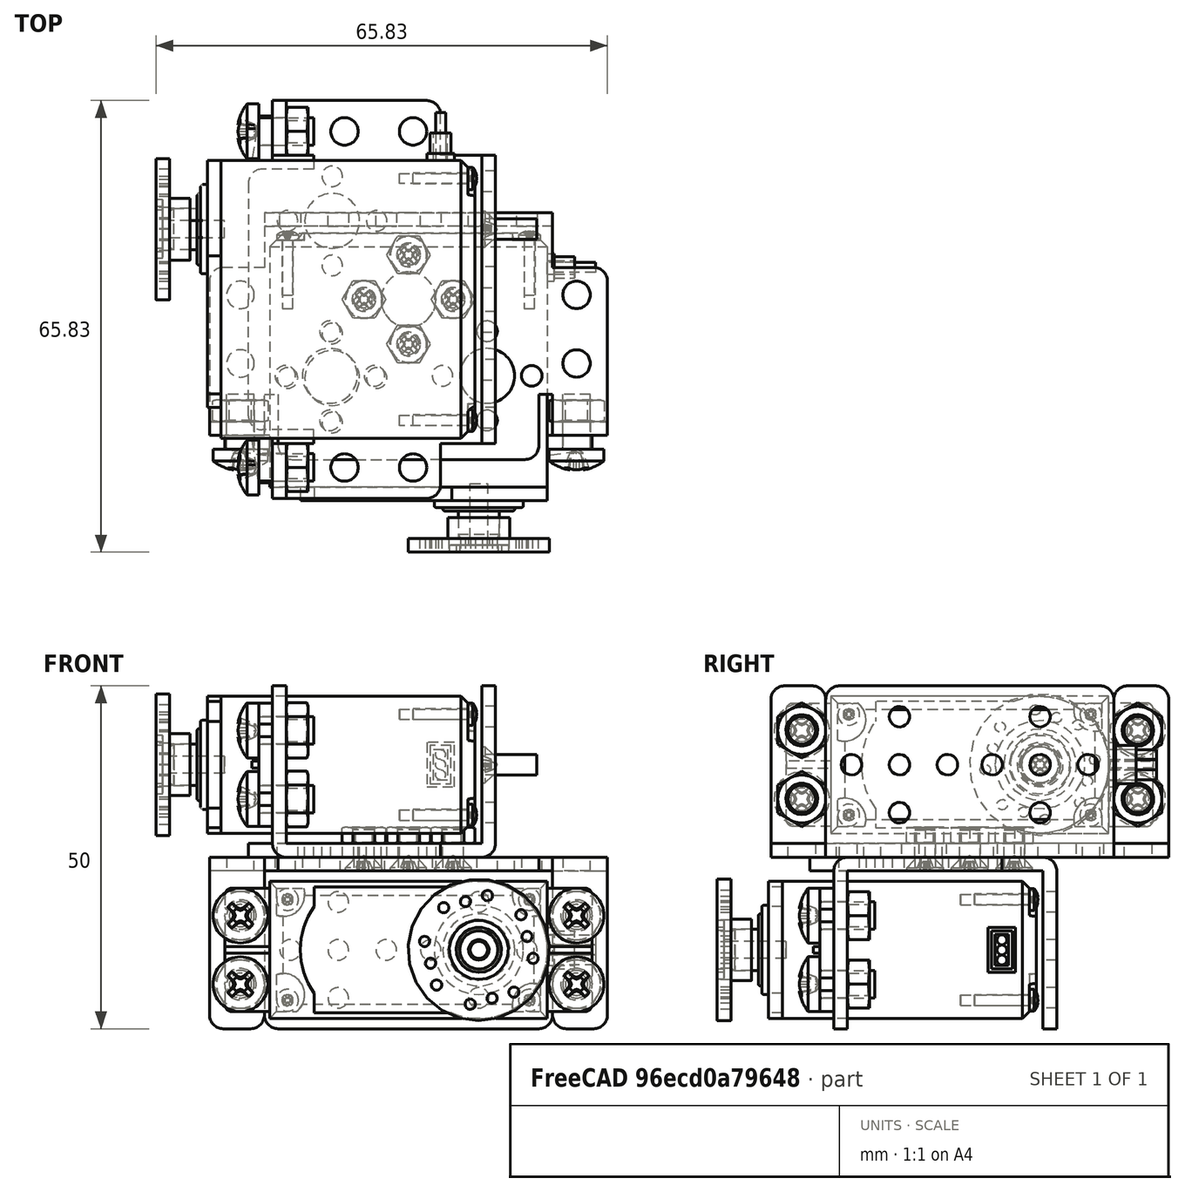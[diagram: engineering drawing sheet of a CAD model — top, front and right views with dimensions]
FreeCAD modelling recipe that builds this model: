
FCSTD DOCUMENT  (FreeCAD 0.19R24276 (Git))
Label: ante_mano
License: All rights reserved
LicenseURL: http://en.wikipedia.org/wiki/All_rights_reserved
objects: Part::FeaturePython×31, App::FeaturePython×24, App::DocumentObjectGroup×6
note: 31 computed .brp shape members not serialized (recipe doc carries the construction recipe); baked Part::Feature solids carry a one-line shape summary decoded from their .brp

FEATURE [Part::FeaturePython] b_parte_servos_001_  label="parte_servos_001"  # a2plus imported part (geometry in sourceFile) (typed FeaturePython)
  Placement = pos=(0,0,0) rot=(-1,0,0;3.14159rad)
  a2p_Version = V0.1
  fixedPosition = true
  objectType = a2pPart
  sourceFile = .\..\piezas\parte_servos.FCStd
  subassemblyImport = false
  timeLastImport = 1.62041e+09
  updateColors = true
FEATURE [Part::FeaturePython] b_parte_servos_001_001  label="parte_servos_002"  # a2plus imported part (geometry in sourceFile) (typed FeaturePython)
  Placement = pos=(-5.32887,5.32887,-1.3e-15) rot=(0,0,1;1.5708rad)
  a2p_Version = V0.1
  fixedPosition = false
  objectType = a2pPart
  sourceFile = .\..\piezas\parte_servos.FCStd
  subassemblyImport = false
  timeLastImport = 1.62041e+09
  updateColors = true
FEATURE [Part::FeaturePython] b_servo_001_  label="servo_001"  # a2plus imported part (geometry in sourceFile) (typed FeaturePython)
  Placement = pos=(2.47451e-08,15,-13.5) rot=(0,-0.707107,0.707107;3.14159rad)
  a2p_Version = V0.1
  fixedPosition = false
  objectType = a2pPart
  sourceFile = .\..\piezas\servo.FCStd
  subassemblyImport = false
  timeLastImport = 1.62041e+09
  updateColors = true
FEATURE [Part::FeaturePython] b_tapa_001_  label="tapa_001"  # a2plus imported part (geometry in sourceFile) (typed FeaturePython)
  Placement = pos=(10.25,-31.5,-13.5) rot=(-0.680531,0.518111,0.518111;1.94651rad)
  a2p_Version = V0.1
  fixedPosition = false
  objectType = a2pPart
  sourceFile = .\..\piezas\tapa.FCStd
  subassemblyImport = false
  timeLastImport = 1.62041e+09
  updateColors = true
FEATURE [App::FeaturePython] planeCoincident_002  label="planeCoincident_002__servo_001"  # a2plus constraint (typed FeaturePython)
  Object1 = b_tapa_001_
  Object2 = b_servo_001_
  ParentTreeObject = -> b_tapa_001_
  SubElement1 = Face23
  SubElement2 = Face7
  Suppressed = false
  Type = plane
  directionConstraint = 1
  offset = 0
FEATURE [App::FeaturePython] planeCoincident_002_mirror  label="planeCoincident_002__tapa_001"  # a2plus constraint (typed FeaturePython)
  Object1 = b_tapa_001_
  Object2 = b_servo_001_
  ParentTreeObject = -> b_servo_001_
  SubElement1 = Face23
  SubElement2 = Face7
  Suppressed = false
  Type = plane
  directionConstraint = 1
  offset = 0
FEATURE [App::FeaturePython] axisCoincident_002  label="axisCoincident_002__servo_001"  # a2plus constraint (typed FeaturePython)
  Object1 = b_tapa_001_
  Object2 = b_servo_001_
  ParentTreeObject = -> b_tapa_001_
  SubElement1 = Face21
  SubElement2 = Face3
  Suppressed = false
  Type = axial
  directionConstraint = 1
  lockRotation = false
FEATURE [App::FeaturePython] axisCoincident_002_mirror  label="axisCoincident_002__tapa_001"  # a2plus constraint (typed FeaturePython)
  Object1 = b_tapa_001_
  Object2 = b_servo_001_
  ParentTreeObject = -> b_servo_001_
  SubElement1 = Face21
  SubElement2 = Face3
  Suppressed = false
  Type = axial
  directionConstraint = 1
  lockRotation = false
FEATURE [App::FeaturePython] planeCoincident_003  label="planeCoincident_003__parte_servos_001"  # a2plus constraint (typed FeaturePython)
  Object1 = b_parte_servos_001_001
  Object2 = b_parte_servos_001_
  ParentTreeObject = -> b_parte_servos_001_001
  SubElement1 = Face8
  SubElement2 = Face8
  Suppressed = false
  Type = plane
  directionConstraint = 1
  offset = 0
FEATURE [App::FeaturePython] planeCoincident_003_mirror  label="planeCoincident_003__parte_servos_002"  # a2plus constraint (typed FeaturePython)
  Object1 = b_parte_servos_001_001
  Object2 = b_parte_servos_001_
  ParentTreeObject = -> b_parte_servos_001_
  SubElement1 = Face8
  SubElement2 = Face8
  Suppressed = false
  Type = plane
  directionConstraint = 1
  offset = 0
FEATURE [App::FeaturePython] axisCoincident_001  label="axisCoincident_001__servo_001"  # a2plus constraint (typed FeaturePython)
  Object1 = b_parte_servos_001_
  Object2 = b_servo_001_
  ParentTreeObject = -> b_parte_servos_001_
  SubElement1 = Face82
  SubElement2 = Face81
  Suppressed = false
  Type = axial
  directionConstraint = 0
  lockRotation = false
FEATURE [App::FeaturePython] axisCoincident_001_mirror  label="axisCoincident_001__parte_servos_001"  # a2plus constraint (typed FeaturePython)
  Object1 = b_parte_servos_001_
  Object2 = b_servo_001_
  ParentTreeObject = -> b_servo_001_
  SubElement1 = Face82
  SubElement2 = Face81
  Suppressed = false
  Type = axial
  directionConstraint = 0
  lockRotation = false
FEATURE [App::FeaturePython] axisCoincident_005  label="axisCoincident_005__parte_servos_001"  # a2plus constraint (typed FeaturePython)
  Object1 = b_servo_001_
  Object2 = b_parte_servos_001_
  ParentTreeObject = -> b_servo_001_
  SubElement1 = Face64
  SubElement2 = Face74
  Suppressed = false
  Type = axial
  directionConstraint = 0
  lockRotation = false
FEATURE [App::FeaturePython] axisCoincident_005_mirror  label="axisCoincident_005__servo_001"  # a2plus constraint (typed FeaturePython)
  Object1 = b_servo_001_
  Object2 = b_parte_servos_001_
  ParentTreeObject = -> b_parte_servos_001_
  SubElement1 = Face64
  SubElement2 = Face74
  Suppressed = false
  Type = axial
  directionConstraint = 0
  lockRotation = false
FEATURE [Part::FeaturePython] b_servo_001_001  label="servo_002"  # a2plus imported part (geometry in sourceFile) (typed FeaturePython)
  Placement = pos=(9.67113,5.32887,13.5) rot=(-0.57735,0.57735,0.57735;4.18879rad)
  a2p_Version = V0.1
  fixedPosition = false
  objectType = a2pPart
  sourceFile = .\..\piezas\servo.FCStd
  subassemblyImport = false
  timeLastImport = 1.62041e+09
  updateColors = true
FEATURE [Part::FeaturePython] b_tapa_001_001  label="tapa_002"  # a2plus imported part (geometry in sourceFile) (typed FeaturePython)
  Placement = pos=(-36.8289,15.5789,13.5) rot=(0.631714,-0.449306,0.631714;3.98615rad)
  a2p_Version = V0.1
  fixedPosition = false
  objectType = a2pPart
  sourceFile = .\..\piezas\tapa.FCStd
  subassemblyImport = false
  timeLastImport = 1.62041e+09
  updateColors = true
FEATURE [App::FeaturePython] planeCoincident_001  label="planeCoincident_001__servo_002"  # a2plus constraint (typed FeaturePython)
  Object1 = b_parte_servos_001_001
  Object2 = b_servo_001_001
  ParentTreeObject = -> b_parte_servos_001_001
  SubElement1 = Face84
  SubElement2 = Face34
  Suppressed = false
  Type = plane
  directionConstraint = 1
  offset = 0
FEATURE [App::FeaturePython] planeCoincident_001_mirror  label="planeCoincident_001__parte_servos_002"  # a2plus constraint (typed FeaturePython)
  Object1 = b_parte_servos_001_001
  Object2 = b_servo_001_001
  ParentTreeObject = -> b_servo_001_001
  SubElement1 = Face84
  SubElement2 = Face34
  Suppressed = false
  Type = plane
  directionConstraint = 1
  offset = 0
FEATURE [App::FeaturePython] planeCoincident_004  label="planeCoincident_004__tapa_002"  # a2plus constraint (typed FeaturePython)
  Object1 = b_servo_001_001
  Object2 = b_tapa_001_001
  ParentTreeObject = -> b_servo_001_001
  SubElement1 = Face118
  SubElement2 = Face23
  Suppressed = false
  Type = plane
  directionConstraint = 1
  offset = 0
FEATURE [App::FeaturePython] planeCoincident_004_mirror  label="planeCoincident_004__servo_002"  # a2plus constraint (typed FeaturePython)
  Object1 = b_servo_001_001
  Object2 = b_tapa_001_001
  ParentTreeObject = -> b_tapa_001_001
  SubElement1 = Face118
  SubElement2 = Face23
  Suppressed = false
  Type = plane
  directionConstraint = 1
  offset = 0
FEATURE [App::FeaturePython] axisCoincident_008  label="axisCoincident_008__servo_002"  # a2plus constraint (typed FeaturePython)
  Object1 = b_tapa_001_001
  Object2 = b_servo_001_001
  ParentTreeObject = -> b_tapa_001_001
  SubElement1 = Face21
  SubElement2 = Face3
  Suppressed = false
  Type = axial
  directionConstraint = 1
  lockRotation = false
FEATURE [App::FeaturePython] axisCoincident_008_mirror  label="axisCoincident_008__tapa_002"  # a2plus constraint (typed FeaturePython)
  Object1 = b_tapa_001_001
  Object2 = b_servo_001_001
  ParentTreeObject = -> b_servo_001_001
  SubElement1 = Face21
  SubElement2 = Face3
  Suppressed = false
  Type = axial
  directionConstraint = 1
  lockRotation = false
FEATURE [Part::FeaturePython] Screw004  label="M4x8-Screw004"  # Fasteners workbench fastener (typed FeaturePython)
  Placement = pos=(24.5,-16.5,-18.5) rot=(1,0,0;1.5708rad)
  baseObject = -> b_servo_001_ [Edge136]
  diameter = 6
  invert = true
  length = 12
  lengthCustom = 8
  matchOuter = true
  offset = 0
  thread = false
  type = 34
FEATURE [Part::FeaturePython] Screw005  label="M4x8-Screw005"  # Fasteners workbench fastener (typed FeaturePython)
  Placement = pos=(24.5,-16.5,-8.5) rot=(1,0,0;1.5708rad)
  baseObject = -> b_servo_001_ [Edge162]
  diameter = 6
  invert = true
  length = 12
  lengthCustom = 8
  matchOuter = true
  offset = 0
  thread = false
  type = 34
FEATURE [Part::FeaturePython] Screw006  label="M4x8-Screw006"  # Fasteners workbench fastener (typed FeaturePython)
  Placement = pos=(-24.5,-16.5,-18.5) rot=(1,0,0;1.5708rad)
  baseObject = -> b_servo_001_ [Edge606]
  diameter = 6
  invert = false
  length = 12
  lengthCustom = 8
  matchOuter = true
  offset = 0
  thread = false
  type = 34
FEATURE [Part::FeaturePython] Screw007  label="M4x8-Screw007"  # Fasteners workbench fastener (typed FeaturePython)
  Placement = pos=(-24.5,-16.5,-8.5) rot=(1,0,0;1.5708rad)
  baseObject = -> b_servo_001_ [Edge361]
  diameter = 6
  invert = false
  length = 12
  lengthCustom = 8
  matchOuter = true
  offset = 0
  thread = false
  type = 34
FEATURE [App::DocumentObjectGroup] Group003  label="parte2"
  Group = -> [Screw004,Screw005,Screw006,Screw007]
FEATURE [App::FeaturePython] axisCoincident_006  label="axisCoincident_006__parte_servos_002"  # a2plus constraint (typed FeaturePython)
  Object1 = b_servo_001_001
  Object2 = b_parte_servos_001_001
  ParentTreeObject = -> b_servo_001_001
  SubElement1 = Face73
  SubElement2 = Face81
  Suppressed = false
  Type = axial
  directionConstraint = 0
  lockRotation = false
FEATURE [App::FeaturePython] axisCoincident_006_mirror  label="axisCoincident_006__servo_002"  # a2plus constraint (typed FeaturePython)
  Object1 = b_servo_001_001
  Object2 = b_parte_servos_001_001
  ParentTreeObject = -> b_parte_servos_001_001
  SubElement1 = Face73
  SubElement2 = Face81
  Suppressed = false
  Type = axial
  directionConstraint = 0
  lockRotation = false
FEATURE [App::FeaturePython] axisCoincident_007  label="axisCoincident_007__parte_servos_002"  # a2plus constraint (typed FeaturePython)
  Object1 = b_servo_001_001
  Object2 = b_parte_servos_001_001
  ParentTreeObject = -> b_servo_001_001
  SubElement1 = Face64
  SubElement2 = Face74
  Suppressed = false
  Type = axial
  directionConstraint = 0
  lockRotation = false
FEATURE [App::FeaturePython] axisCoincident_007_mirror  label="axisCoincident_007__servo_002"  # a2plus constraint (typed FeaturePython)
  Object1 = b_servo_001_001
  Object2 = b_parte_servos_001_001
  ParentTreeObject = -> b_parte_servos_001_001
  SubElement1 = Face64
  SubElement2 = Face74
  Suppressed = false
  Type = axial
  directionConstraint = 0
  lockRotation = false
FEATURE [App::FeaturePython] axisCoincident_003  label="axisCoincident_003__parte_servos_002"  # a2plus constraint (typed FeaturePython)
  Object1 = b_parte_servos_001_
  Object2 = b_parte_servos_001_001
  ParentTreeObject = -> b_parte_servos_001_
  SubElement1 = Face29
  SubElement2 = Face58
  Suppressed = false
  Type = axial
  directionConstraint = 1
  lockRotation = false
FEATURE [App::FeaturePython] axisCoincident_003_mirror  label="axisCoincident_003__parte_servos_001"  # a2plus constraint (typed FeaturePython)
  Object1 = b_parte_servos_001_
  Object2 = b_parte_servos_001_001
  ParentTreeObject = -> b_parte_servos_001_001
  SubElement1 = Face29
  SubElement2 = Face58
  Suppressed = false
  Type = axial
  directionConstraint = 1
  lockRotation = false
FEATURE [App::FeaturePython] axisCoincident_004  label="axisCoincident_004__parte_servos_001"  # a2plus constraint (typed FeaturePython)
  Object1 = b_parte_servos_001_001
  Object2 = b_parte_servos_001_
  ParentTreeObject = -> b_parte_servos_001_001
  SubElement1 = Face40
  SubElement2 = Face33
  Suppressed = false
  Type = axial
  directionConstraint = 1
  lockRotation = false
FEATURE [App::FeaturePython] axisCoincident_004_mirror  label="axisCoincident_004__parte_servos_002"  # a2plus constraint (typed FeaturePython)
  Object1 = b_parte_servos_001_001
  Object2 = b_parte_servos_001_
  ParentTreeObject = -> b_parte_servos_001_
  SubElement1 = Face40
  SubElement2 = Face33
  Suppressed = false
  Type = axial
  directionConstraint = 1
  lockRotation = false
FEATURE [Part::FeaturePython] Screw  label="M4x8-Screw"  # Fasteners workbench fastener (typed FeaturePython)
  Placement = pos=(-21.8289,29.8289,8.5) rot=(0,-1,0;1.5708rad)
  baseObject = -> b_servo_001_001 [Edge421]
  diameter = 6
  invert = true
  length = 12
  lengthCustom = 8
  matchOuter = true
  offset = 0
  thread = false
  type = 34
FEATURE [Part::FeaturePython] Screw013  label="M4x8-Screw001"  # Fasteners workbench fastener (typed FeaturePython)
  Placement = pos=(-21.8289,-19.1711,8.5) rot=(0,-1,0;1.5708rad)
  baseObject = -> b_servo_001_001 [Edge102]
  diameter = 6
  invert = false
  length = 12
  lengthCustom = 8
  matchOuter = true
  offset = 0
  thread = false
  type = 34
FEATURE [Part::FeaturePython] Screw014  label="M4x8-Screw002"  # Fasteners workbench fastener (typed FeaturePython)
  Placement = pos=(-21.8289,-19.1711,18.5) rot=(0,-1,0;1.5708rad)
  baseObject = -> b_servo_001_001 [Edge88]
  diameter = 6
  invert = false
  length = 12
  lengthCustom = 8
  matchOuter = true
  offset = 0
  thread = false
  type = 34
FEATURE [Part::FeaturePython] Screw015  label="M4x8-Screw003"  # Fasteners workbench fastener (typed FeaturePython)
  Placement = pos=(-21.8289,29.8289,18.5) rot=(0,-1,0;1.5708rad)
  baseObject = -> b_servo_001_001 [Edge395]
  diameter = 6
  invert = true
  length = 12
  lengthCustom = 8
  matchOuter = true
  offset = 0
  thread = false
  type = 34
FEATURE [App::DocumentObjectGroup] Group002  label="parte1"
  Group = -> [Screw,Screw013,Screw014,Screw015]
FEATURE [Part::FeaturePython] Screw016  label="M3x6-Screw"  # Fasteners workbench fastener (typed FeaturePython)
  Placement = pos=(0,11.8289,-2) rot=(-1,0,0;3.14159rad)
  baseObject = -> b_parte_servos_001_ [Edge148]
  diameter = 4
  invert = false
  length = 11
  lengthCustom = 6
  matchOuter = false
  offset = 0
  thread = false
  type = 35
FEATURE [Part::FeaturePython] Screw017  label="M3x6-Screw001"  # Fasteners workbench fastener (typed FeaturePython)
  Placement = pos=(6.5,5.32887,-2) rot=(-1,0,0;3.14159rad)
  baseObject = -> b_parte_servos_001_ [Edge154]
  diameter = 4
  invert = false
  length = 11
  lengthCustom = 6
  matchOuter = false
  offset = 0
  thread = false
  type = 35
FEATURE [Part::FeaturePython] Screw018  label="M3x6-Screw002"  # Fasteners workbench fastener (typed FeaturePython)
  Placement = pos=(0,-1.17113,-2) rot=(-1,0,0;3.14159rad)
  baseObject = -> b_parte_servos_001_ [Edge152]
  diameter = 4
  invert = false
  length = 11
  lengthCustom = 6
  matchOuter = false
  offset = 0
  thread = false
  type = 35
FEATURE [Part::FeaturePython] Screw019  label="M3x6-Screw003"  # Fasteners workbench fastener (typed FeaturePython)
  Placement = pos=(-6.5,5.32887,-2) rot=(-1,0,0;3.14159rad)
  baseObject = -> b_parte_servos_001_ [Edge106]
  diameter = 4
  invert = false
  length = 11
  lengthCustom = 6
  matchOuter = false
  offset = 0
  thread = false
  type = 35
FEATURE [Part::FeaturePython] Nut  label="M4-Nut"  # Fasteners workbench fastener (typed FeaturePython)
  Placement = pos=(-17.8289,-19.1711,8.5) rot=(0,1,0;1.5708rad)
  baseObject = -> b_parte_servos_001_001 [Edge193]
  diameter = 6
  invert = true
  matchOuter = true
  offset = 0
  thread = false
  type = 7
FEATURE [Part::FeaturePython] Nut001  label="M4-Nut001"  # Fasteners workbench fastener (typed FeaturePython)
  Placement = pos=(-17.8289,-19.1711,18.5) rot=(0,1,0;1.5708rad)
  baseObject = -> b_parte_servos_001_001 [Edge192]
  diameter = 6
  invert = true
  matchOuter = true
  offset = 0
  thread = false
  type = 7
FEATURE [Part::FeaturePython] Nut002  label="M4-Nut002"  # Fasteners workbench fastener (typed FeaturePython)
  Placement = pos=(-17.8289,29.8289,8.5) rot=(0,1,0;1.5708rad)
  baseObject = -> b_parte_servos_001_001 [Edge220]
  diameter = 6
  invert = true
  matchOuter = true
  offset = 0
  thread = false
  type = 7
FEATURE [Part::FeaturePython] Nut003  label="M4-Nut003"  # Fasteners workbench fastener (typed FeaturePython)
  Placement = pos=(-17.8289,29.8289,18.5) rot=(0,1,0;1.5708rad)
  baseObject = -> b_parte_servos_001_001 [Edge219]
  diameter = 6
  invert = true
  matchOuter = true
  offset = 0
  thread = false
  type = 7
FEATURE [App::DocumentObjectGroup] Group004  label="parte_1"
  Group = -> [Nut,Nut001,Nut002,Nut003]
FEATURE [Part::FeaturePython] Nut004  label="M3-Nut"  # Fasteners workbench fastener (typed FeaturePython)
  Placement = pos=(6.5,5.32887,2) rot=(0,0,1;0rad)
  baseObject = -> b_parte_servos_001_001 [Edge100]
  diameter = 4
  invert = false
  matchOuter = true
  offset = 0
  thread = false
  type = 7
FEATURE [Part::FeaturePython] Nut005  label="M3-Nut001"  # Fasteners workbench fastener (typed FeaturePython)
  Placement = pos=(5.23036e-07,-1.17113,2) rot=(0,0,1;0rad)
  baseObject = -> b_parte_servos_001_001 [Edge106]
  diameter = 4
  invert = false
  matchOuter = true
  offset = 0
  thread = false
  type = 7
FEATURE [Part::FeaturePython] Nut006  label="M3-Nut002"  # Fasteners workbench fastener (typed FeaturePython)
  Placement = pos=(-6.5,5.32887,2) rot=(0,0,1;0rad)
  baseObject = -> b_parte_servos_001_001 [Edge104]
  diameter = 4
  invert = false
  matchOuter = true
  offset = 0
  thread = false
  type = 7
FEATURE [Part::FeaturePython] Nut007  label="M3-Nut003"  # Fasteners workbench fastener (typed FeaturePython)
  Placement = pos=(6.88169e-07,11.8289,2) rot=(0,0,1;0rad)
  baseObject = -> b_parte_servos_001_001 [Edge154]
  diameter = 4
  invert = false
  matchOuter = true
  offset = 0
  thread = false
  type = 7
FEATURE [Part::FeaturePython] Nut008  label="M4-Nut004"  # Fasteners workbench fastener (typed FeaturePython)
  Placement = pos=(24.5,-12.5,-8.5) rot=(-1,0,0;1.5708rad)
  baseObject = -> b_parte_servos_001_ [Edge220]
  diameter = 6
  invert = true
  matchOuter = true
  offset = 0
  thread = false
  type = 7
FEATURE [Part::FeaturePython] Nut009  label="M4-Nut005"  # Fasteners workbench fastener (typed FeaturePython)
  Placement = pos=(24.5,-12.5,-18.5) rot=(-1,0,0;1.5708rad)
  baseObject = -> b_parte_servos_001_ [Edge219]
  diameter = 6
  invert = true
  matchOuter = true
  offset = 0
  thread = false
  type = 7
FEATURE [Part::FeaturePython] Nut010  label="M4-Nut006"  # Fasteners workbench fastener (typed FeaturePython)
  Placement = pos=(-24.5,-12.5,-18.5) rot=(-1,0,0;1.5708rad)
  baseObject = -> b_parte_servos_001_ [Edge192]
  diameter = 6
  invert = true
  matchOuter = true
  offset = 0
  thread = false
  type = 7
FEATURE [Part::FeaturePython] Nut011  label="M4-Nut007"  # Fasteners workbench fastener (typed FeaturePython)
  Placement = pos=(-24.5,-12.5,-8.5) rot=(-1,0,0;1.5708rad)
  baseObject = -> b_parte_servos_001_ [Edge193]
  diameter = 6
  invert = true
  matchOuter = true
  offset = 0
  thread = false
  type = 7
FEATURE [App::DocumentObjectGroup] Group005  label="parte_2"
  Group = -> [Nut008,Nut009,Nut010,Nut011]
FEATURE [App::DocumentObjectGroup] Group001  label="tuercas"
  Group = -> [Group004,Group005,Nut004,Nut005,Nut006,Nut007]
FEATURE [Part::FeaturePython] Screw020  label="M3x8-Screw"  # Fasteners workbench fastener (typed FeaturePython)
  Placement = pos=(10.6711,15.5789,13.5) rot=(0,-1,0;1.5708rad)
  baseObject = -> b_parte_servos_001_001 [Edge83]
  diameter = 4
  invert = false
  length = 3
  lengthCustom = 8
  matchOuter = false
  offset = 0
  thread = false
  type = 35
FEATURE [App::DocumentObjectGroup] Group  label="tornillos"
  Group = -> [Group002,Group003,Screw016,Screw017,Screw018,Screw019,Screw020]
